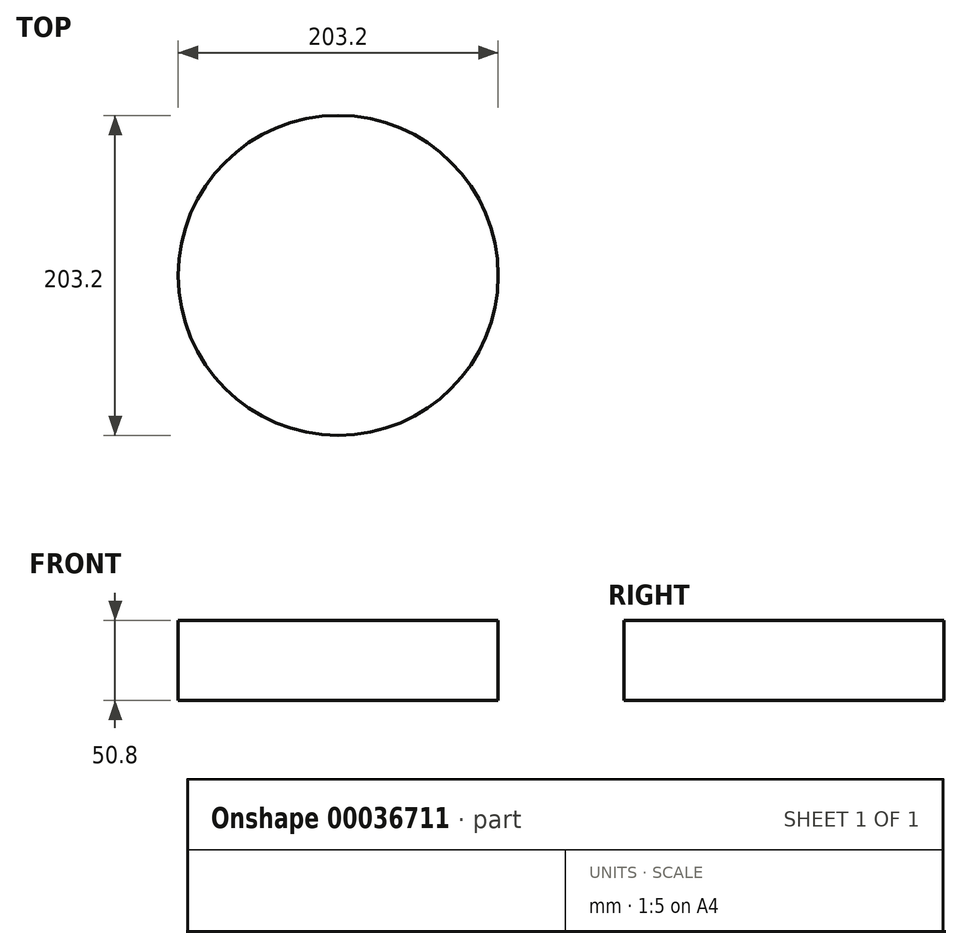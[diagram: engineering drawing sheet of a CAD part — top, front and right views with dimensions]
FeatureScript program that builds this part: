
annotation { "Feature Type Name" : "Feature", "Feature Type Description" : "" }
export const myFeature = defineFeature(function(context is Context, id is Id, definition is map)
    precondition{}
    {
        {
            var Q0;
            Q0=qCreatedBy(makeId("Front.planeOp"),FACE);
            var sketch = newSketch(context, id + "F0", { "sketchPlane" : qUnion([Q0])});
            skLineSegment(sketch, "E0.bottom", {"start": v(0, 0) * mm, "end": v(101.6, 0) * mm});
            skLineSegment(sketch, "E0.top", {"start": v(0, 50.8) * mm, "end": v(101.6, 50.8) * mm});
            skLineSegment(sketch, "E0.left", {"start": v(0, 0) * mm, "end": v(0, 50.8) * mm});
            skLineSegment(sketch, "E0.right", {"start": v(101.6, 0) * mm, "end": v(101.6, 50.8) * mm});
            skSolve(sketch);
        }
        {
            var Q0;
            Q0=makeQuery(id+"F0.imprint","IMPRINT",FACE,{"disambiguationData":[TD([[makeQuery(id+"F0.imprint","IMPRINT",EDGE,{"derivedFrom":sQuery(id+"F0.wireOp",EDGE,"E0.bottom")}),1.0]])]});
            var Q1;
            Q1=sQuery(id+"F0.wireOp",EDGE,"E0.left");
            revolve(context, id + "F1", {"entities" : qUnion([Q0]), "axis" : qUnion([Q1]), "revolveType" : RevolveType.FULL});
        }
    });
